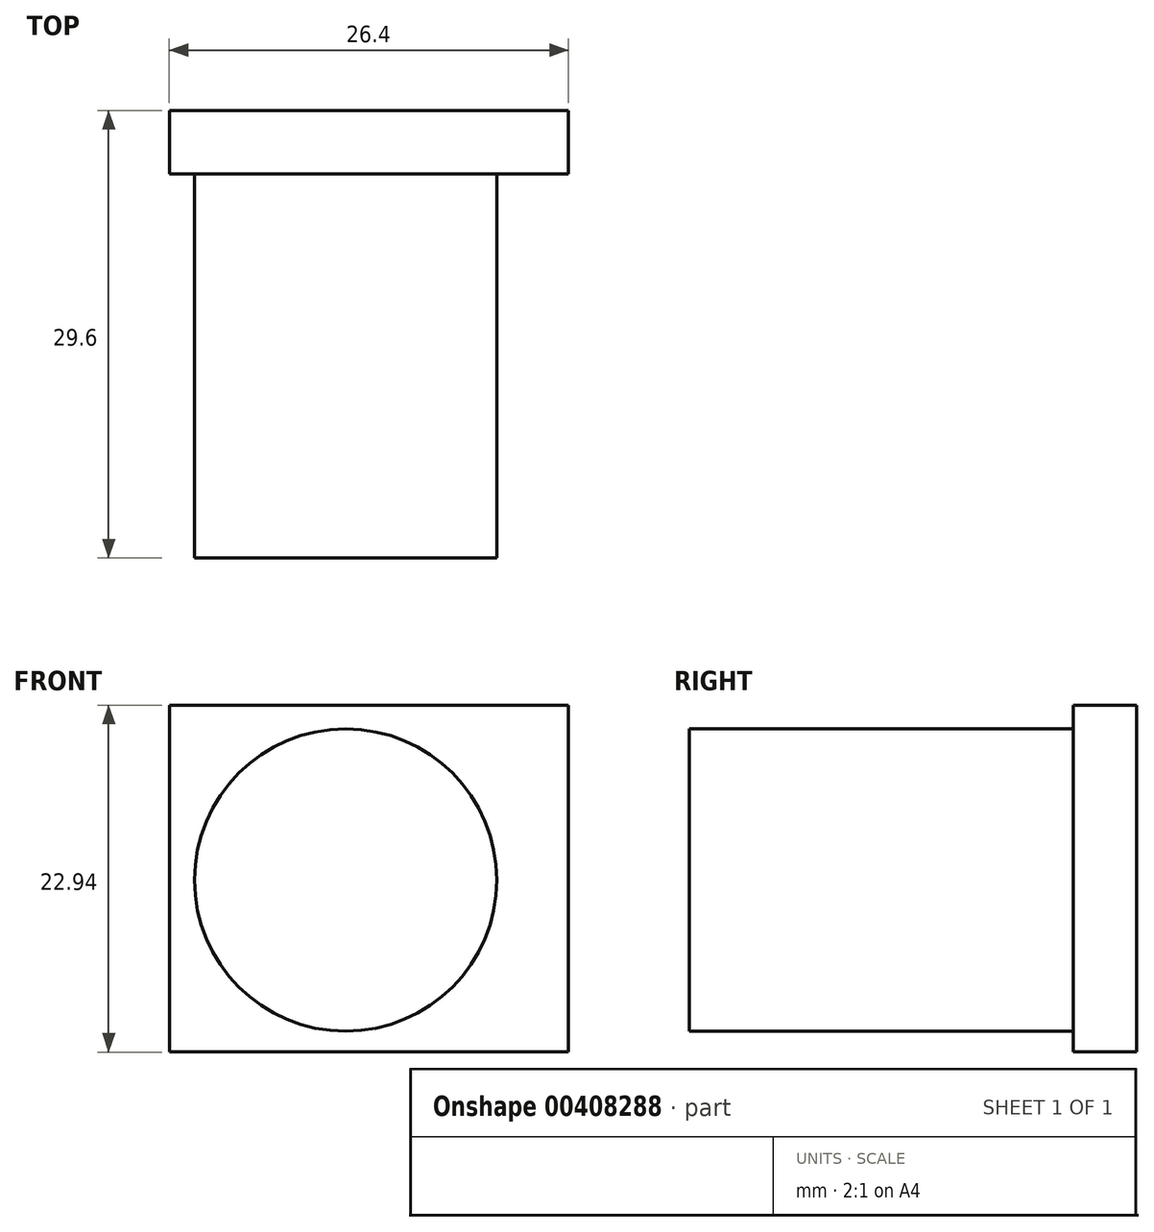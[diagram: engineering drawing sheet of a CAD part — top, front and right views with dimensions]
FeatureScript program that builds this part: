
annotation { "Feature Type Name" : "Feature", "Feature Type Description" : "" }
export const myFeature = defineFeature(function(context is Context, id is Id, definition is map)
    precondition{}
    {
        {
            var Q0;
            Q0=qCreatedBy(makeId("Front.planeOp"),FACE);
            var sketch = newSketch(context, id + "F0", { "sketchPlane" : qUnion([Q0])});
            skCircle(sketch, "E0", {"center": v(0, 0) * mm, "radius": 10 * mm});
            skSolve(sketch);
        }
        {
            var Q0;
            Q0 = qSketchRegion(id + "F0", true);
            extrude(context, id + "F1", {"entities" : qUnion([Q0]), "depth" : 25.4 * mm});
        }
        {
            var Q0;
            Q0=qCreatedBy(makeId("Front.planeOp"),FACE);
            var sketch = newSketch(context, id + "F2", { "sketchPlane" : qUnion([Q0])});
            skLineSegment(sketch, "E1.bottom", {"start": v(-11.67, 11.56) * mm, "end": v(14.73, 11.56) * mm});
            skLineSegment(sketch, "E1.top", {"start": v(-11.67, -11.38) * mm, "end": v(14.73, -11.38) * mm});
            skLineSegment(sketch, "E1.left", {"start": v(-11.67, 11.56) * mm, "end": v(-11.67, -11.38) * mm});
            skLineSegment(sketch, "E1.right", {"start": v(14.73, 11.56) * mm, "end": v(14.73, -11.38) * mm});
            skSolve(sketch);
        }
        {
            var Q0;
            Q0=makeQuery(id+"F2.imprint","IMPRINT",FACE,{"disambiguationData":[TD([[makeQuery(id+"F2.imprint","IMPRINT",EDGE,{"derivedFrom":sQuery(id+"F2.wireOp",EDGE,"E1.bottom")}),-1.0]])]});
            extrude(context, id + "F3", {"entities" : qUnion([Q0]), "operationType" : NewBodyOperationType.ADD, "oppositeDirection" : true, "depth" : 4.2 * mm});
        }
    });
